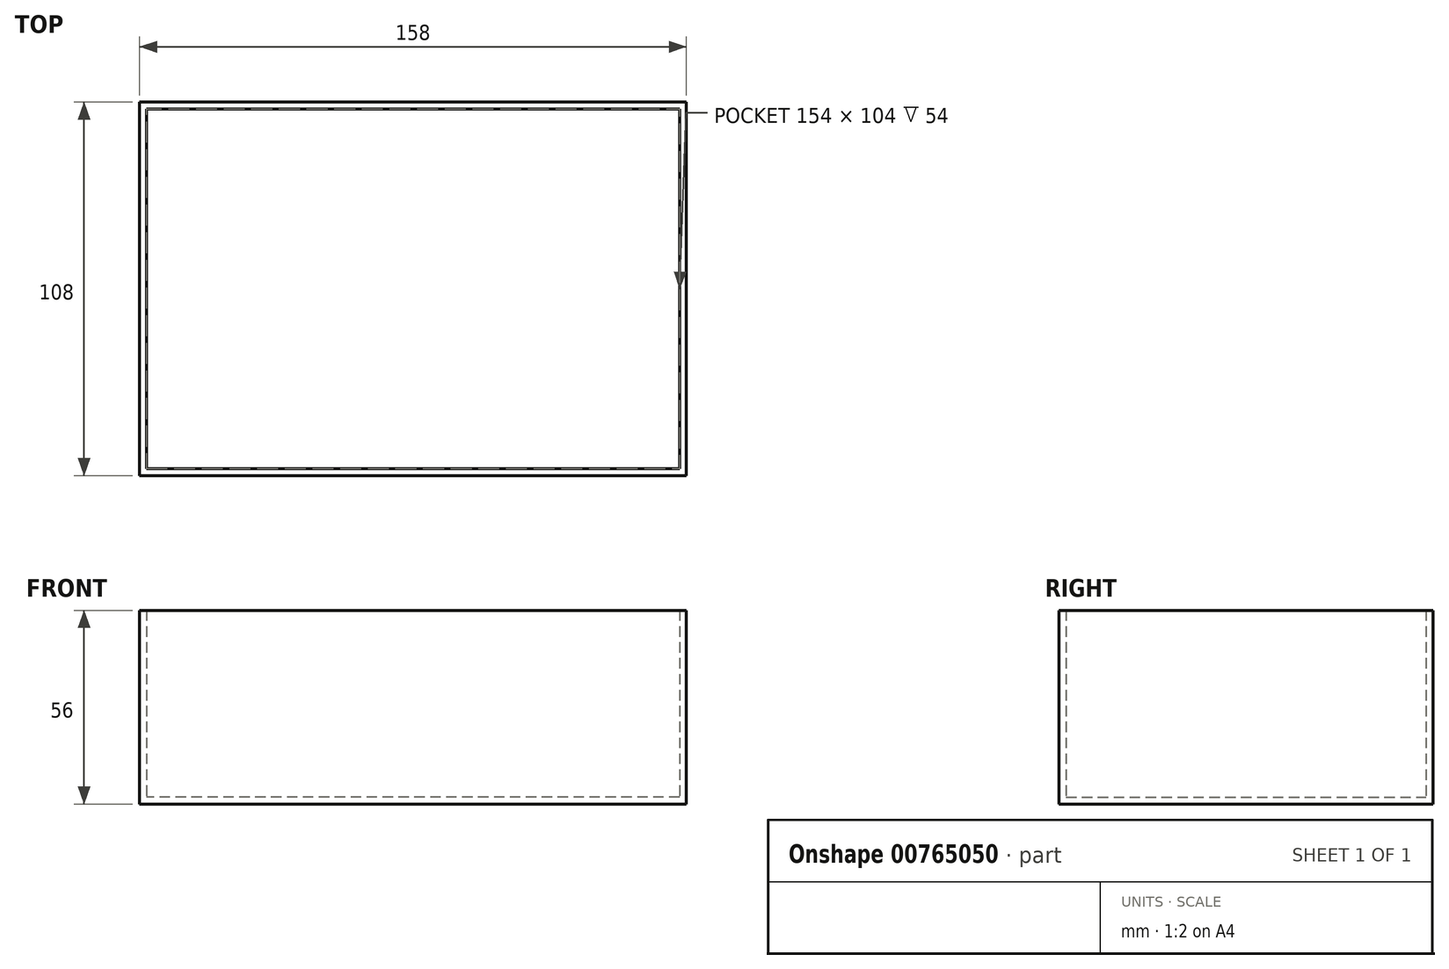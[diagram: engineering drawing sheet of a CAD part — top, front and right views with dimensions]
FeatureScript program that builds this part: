
annotation { "Feature Type Name" : "Feature", "Feature Type Description" : "" }
export const myFeature = defineFeature(function(context is Context, id is Id, definition is map)
    precondition{}
    {
        {
            var Q0;
            Q0=qCreatedBy(makeId("Top.planeOp"),FACE);
            var sketch = newSketch(context, id + "F0", { "sketchPlane" : qUnion([Q0])});
            skLineSegment(sketch, "E0.bottom", {"start": v(77, -52) * mm, "end": v(-77, -52) * mm});
            skLineSegment(sketch, "E0.top", {"start": v(77, 52) * mm, "end": v(-77, 52) * mm});
            skLineSegment(sketch, "E0.left", {"start": v(77, -52) * mm, "end": v(77, 52) * mm});
            skLineSegment(sketch, "E0.right", {"start": v(-77, -52) * mm, "end": v(-77, 52) * mm});
            skPoint(sketch, "E0.middle", {"position": v(0, 0) * mm});
            skLineSegment(sketch, "E1.0", {"start": v(79, 54) * mm, "end": v(-79, 54) * mm});
            skLineSegment(sketch, "E1.1", {"start": v(79, -54) * mm, "end": v(79, 54) * mm});
            skLineSegment(sketch, "E1.2", {"start": v(79, -54) * mm, "end": v(-79, -54) * mm});
            skLineSegment(sketch, "E1.3", {"start": v(-79, -54) * mm, "end": v(-79, 54) * mm});
            skSolve(sketch);
        }
        {
            var Q0;
            Q0=makeQuery(id+"F0.imprint","IMPRINT",FACE,{"disambiguationData":[TD([[makeQuery(id+"F0.imprint","IMPRINT",EDGE,{"derivedFrom":sQuery(id+"F0.wireOp",EDGE,"E0.bottom")}),1.0]])]});
            var Q1;
            Q1=makeQuery(id+"F0.imprint","IMPRINT",FACE,{"disambiguationData":[TD([[makeQuery(id+"F0.imprint","IMPRINT",EDGE,{"derivedFrom":sQuery(id+"F0.wireOp",EDGE,"E0.bottom")}),-1.0]])]});
            extrude(context, id + "F1", {"entities" : qUnion([Q0, Q1]), "oppositeDirection" : true, "depth" : 2 * mm, "offsetDistance" : 25 * mm});
        }
        {
            var Q0;
            Q0=makeQuery(id+"F0.imprint","IMPRINT",FACE,{"disambiguationData":[TD([[makeQuery(id+"F0.imprint","IMPRINT",EDGE,{"derivedFrom":sQuery(id+"F0.wireOp",EDGE,"E0.bottom")}),1.0]])]});
            extrude(context, id + "F2", {"entities" : qUnion([Q0]), "operationType" : NewBodyOperationType.ADD, "depth" : 54 * mm, "offsetDistance" : 25 * mm});
        }
    });
